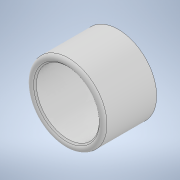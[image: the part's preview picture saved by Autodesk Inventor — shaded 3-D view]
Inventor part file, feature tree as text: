
AUTODESK INVENTOR PART (.ipt)
format: ipt  version: 2020 (Build 240168000, 168)  size: 144,896 bytes
history: native  units: in
note: dims shown in document units (in); Inventor stores cm internally (conversion verified against a paired STEP export)
features: sketch x4, extrude x3, fillet x3
ambient origin geometry x8: Origin, YZ Plane, XZ Plane, XY Plane, X Axis, Y Axis, Z Axis, Center Point
bodies: Solid1 (feature_tree)
feature tree (10):
  extrude  "Extrusion1"  Depth=1.0in
  sketch  "Sketch2"  dims[d3=1.0in d4=0.0in d5=1.1in]
  extrude  "Extrusion2"  Depth=1.0in
  extrude  "Extrusion3"  Depth=0.125in
  fillet  "Fillet1"  Radius=0.125in
  fillet  "Fillet2"  Radius=0.05in
  fillet  "Fillet3"  [1 undecoded]
  sketch  "Sketch1"  dims[d0=1.0in d1=0.0in d2=1.0in]
  sketch  "Sketch3"  dims[d6=0.2in d7=0.0in d8=0.125in d9=0.125in d10=0.05in]
  sketch  "Sketch4"
note: 1 required parameter value undecoded (feature->parameter linkage not recoverable at this tier; creation-order binding heuristic only, values carry confidence <= 0.55)
